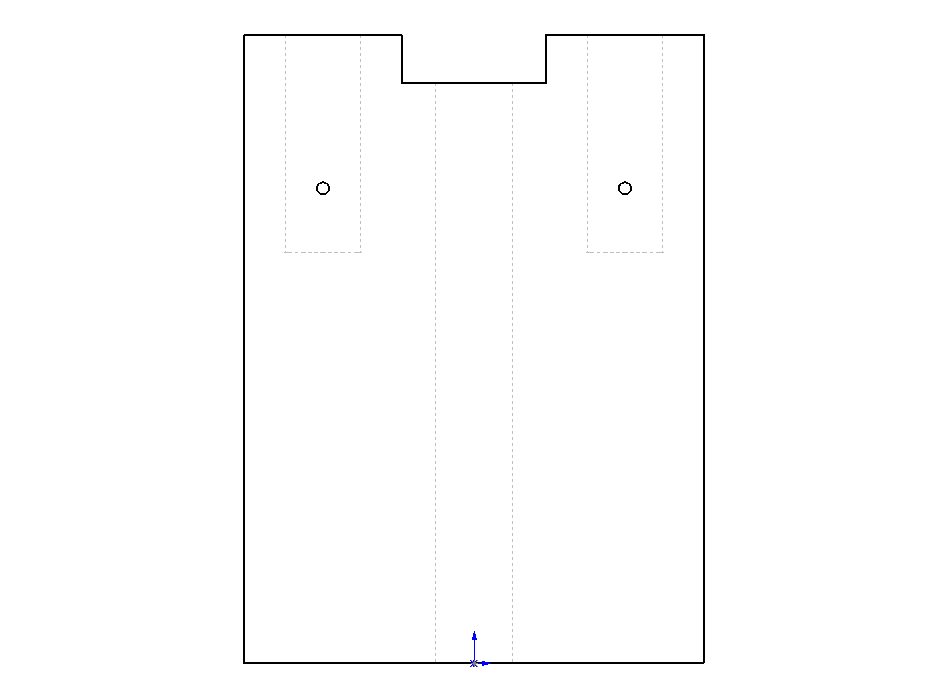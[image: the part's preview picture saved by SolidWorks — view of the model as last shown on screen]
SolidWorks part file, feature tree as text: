
SOLIDWORKS PART (.sldprt)
format: sldprt  version: not decoded by parser v0  size: 733,696 bytes
history: native  units: mm
features: sketch x6, cut_extrude x3, material x1, extrude x1, hole x1 + 1 further entry (+11 scaffold rows collapsed)
feature tree (24):
  scaffold x11  (default folders/planes/origin — collapsed)
  material  "Material <not specified>"
  "Origin"  ID=-1
  sketch  "Sketch1"  dims[D1=52.0mm D2=38.0mm]
  extrude  "Extrude1"  Depth=15mm
  sketch  "Sketch3"  dims[c1.D1=6.35mm c1.D2=4.1656mm c1.D3=4.1656mm c2.D2=25.0mm c2.D3=7.5mm]
  cut_extrude  "Cut-Extrude2"  Depth=18mm
  sketch  "Sketch5"  dims[D1=12.0mm]
  cut_extrude  "Cut-Extrude4"  Depth=4mm
  hole  "1/4 Clearance Hole1"  Diameter=6.5278mm Depth=48mm
  sketch  "Sketch11"  dims[D1=7.5mm]
  sketch  "Sketch10"  dims[hole-wizard template sketch: 60 standard entries collapsed; hole parameters kept: c18.Thru Hole Depth=48.0mm]
  sketch  "Sketch12"  dims[D1=1.016mm D2=12.7mm]
  cut_extrude  "Cut-Extrude5"  [1 undecoded]
decode coverage: 10 of 11 modeling features carry decoded parameters; 1 rows unclassified (native names shown)
note: ~ marks probable driven/reference dimensions
note: 1 parameter value undecoded
note: suppression state not decoded; provenance and decode notes live in map.json
